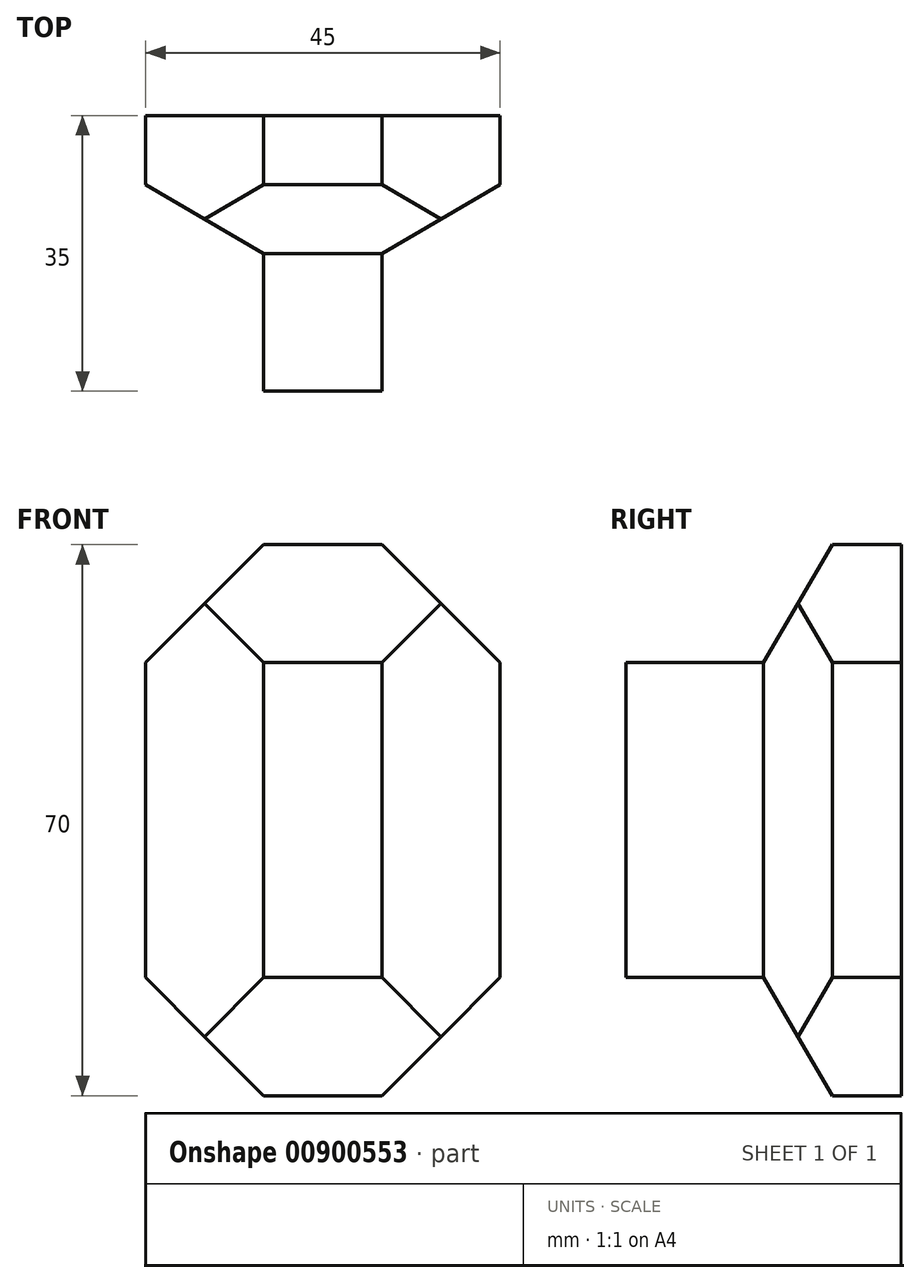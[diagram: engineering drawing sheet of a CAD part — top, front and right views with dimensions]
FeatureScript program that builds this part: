
annotation { "Feature Type Name" : "Feature", "Feature Type Description" : "" }
export const myFeature = defineFeature(function(context is Context, id is Id, definition is map)
    precondition{}
    {
        {
            var Q0;
            Q0=qCreatedBy(makeId("Top.planeOp"),FACE);
            var sketch = newSketch(context, id + "F0", { "sketchPlane" : qUnion([Q0])});
            skLineSegment(sketch, "E0.bottom", {"start": v(7.5, 17.5) * mm, "end": v(-7.5, 17.5) * mm});
            skLineSegment(sketch, "E0.top", {"start": v(7.5, -17.5) * mm, "end": v(-7.5, -17.5) * mm});
            skLineSegment(sketch, "E0.left", {"start": v(7.5, 17.5) * mm, "end": v(7.5, -17.5) * mm});
            skLineSegment(sketch, "E0.right", {"start": v(-7.5, 17.5) * mm, "end": v(-7.5, -17.5) * mm});
            skPoint(sketch, "E0.middle", {"position": v(0, 0) * mm});
            skLineSegment(sketch, "E1.bottom", {"start": v(-7.5, 17.5) * mm, "end": v(22.5, 17.5) * mm});
            skLineSegment(sketch, "E1.top", {"start": v(-7.5, 0) * mm, "end": v(22.5, 0) * mm});
            skLineSegment(sketch, "E1.left", {"start": v(-7.5, 17.5) * mm, "end": v(-7.5, 0) * mm});
            skLineSegment(sketch, "E1.right", {"start": v(22.5, 17.5) * mm, "end": v(22.5, 0) * mm});
            skLineSegment(sketch, "E2.bottom", {"start": v(7.5, 17.5) * mm, "end": v(-22.5, 17.5) * mm});
            skLineSegment(sketch, "E2.top", {"start": v(7.5, 0) * mm, "end": v(-22.5, 0) * mm});
            skLineSegment(sketch, "E2.left", {"start": v(7.5, 17.5) * mm, "end": v(7.5, 0) * mm});
            skLineSegment(sketch, "E2.right", {"start": v(-22.5, 17.5) * mm, "end": v(-22.5, 0) * mm});
            skLineSegment(sketch, "E3.bottom", {"start": v(-22.5, 17.5) * mm, "end": v(22.5, 17.5) * mm});
            skLineSegment(sketch, "E3.top", {"start": v(-22.5, 8.75) * mm, "end": v(22.5, 8.75) * mm});
            skLineSegment(sketch, "E3.left", {"start": v(-22.5, 17.5) * mm, "end": v(-22.5, 8.75) * mm});
            skLineSegment(sketch, "E3.right", {"start": v(22.5, 17.5) * mm, "end": v(22.5, 8.75) * mm});
            skLineSegment(sketch, "E4", {"start": v(-22.5, 8.75) * mm, "end": v(-7.5, 0) * mm});
            skLineSegment(sketch, "E5", {"start": v(22.5, 8.75) * mm, "end": v(7.5, 0) * mm});
            skSolve(sketch);
        }
        {
            var Q0;
            {var subQ0=sQuery(id+"F0.wireOp",EDGE,"E0.bottom");Q0=makeQuery(id+"F0.imprint","IMPRINT",FACE,{"disambiguationData":[TD([[makeQuery(id+"F0.imprint","IMPRINT",EDGE,{"derivedFrom":subQ0}),1.0]])]});}
            var Q1;
            {var subQ0=sQuery(id+"F0.wireOp",EDGE,"E0.top");Q1=makeQuery(id+"F0.imprint","IMPRINT",FACE,{"disambiguationData":[TD([[makeQuery(id+"F0.imprint","IMPRINT",EDGE,{"derivedFrom":subQ0}),-1.0]])]});}
            var Q2;
            {var subQ3=sQuery(id+"F0.wireOp",EDGE,"E3.top");var subQ5=sQuery(id+"F0.wireOp",EDGE,"E0.right");var subQ7=makeQuery(id+"F0.imprint","INTERSECT",VERTEX,{"derivedFrom":[subQ5,subQ3]});Q2=makeQuery(id+"F0.imprint","IMPRINT",FACE,{"disambiguationData":[TD([[makeQuery(id+"F0.imprint","IMPRINT",EDGE,{"disambiguationData":[TD([[subQ7,-1.0]])],"derivedFrom":subQ3}),-1.0]])]});}
            var Q3;
            {var subQ0=sQuery(id+"F0.wireOp",EDGE,"E1.bottom");Q3=makeQuery(id+"F0.imprint","IMPRINT",FACE,{"disambiguationData":[TD([[makeQuery(id+"F0.imprint","IMPRINT",EDGE,{"derivedFrom":subQ0}),-1.0]])]});}
            var Q4;
            {var subQ0=sQuery(id+"F0.wireOp",EDGE,"E5");Q4=makeQuery(id+"F0.imprint","IMPRINT",FACE,{"disambiguationData":[TD([[makeQuery(id+"F0.imprint","IMPRINT",EDGE,{"derivedFrom":subQ0}),-1.0]])]});}
            var Q5;
            {var subQ0=sQuery(id+"F0.wireOp",EDGE,"E2.bottom");Q5=makeQuery(id+"F0.imprint","IMPRINT",FACE,{"disambiguationData":[TD([[makeQuery(id+"F0.imprint","IMPRINT",EDGE,{"derivedFrom":subQ0}),1.0]])]});}
            var Q6;
            {var subQ0=sQuery(id+"F0.wireOp",EDGE,"E4");Q6=makeQuery(id+"F0.imprint","IMPRINT",FACE,{"disambiguationData":[TD([[makeQuery(id+"F0.imprint","IMPRINT",EDGE,{"derivedFrom":subQ0}),1.0]])]});}
            extrude(context, id + "F1", {"entities" : qUnion([Q0, Q1, Q2, Q3, Q4, Q5, Q6]), "depth" : 40 * mm, "offsetDistance" : 25 * mm});
        }
        {
            var Q0;
            {var subQ3=sQuery(id+"F0.wireOp",EDGE,"E3.top");var subQ5=sQuery(id+"F0.wireOp",EDGE,"E0.right");var subQ7=makeQuery(id+"F0.imprint","INTERSECT",VERTEX,{"derivedFrom":[subQ5,subQ3]});Q0=makeQuery(id+"F0.imprint","IMPRINT",FACE,{"disambiguationData":[TD([[makeQuery(id+"F0.imprint","IMPRINT",EDGE,{"disambiguationData":[TD([[subQ7,-1.0]])],"derivedFrom":subQ3}),-1.0]])]});}
            var Q1;
            {var subQ0=sQuery(id+"F0.wireOp",EDGE,"E0.bottom");Q1=makeQuery(id+"F0.imprint","IMPRINT",FACE,{"disambiguationData":[TD([[makeQuery(id+"F0.imprint","IMPRINT",EDGE,{"derivedFrom":subQ0}),1.0]])]});}
            extrude(context, id + "F2", {"entities" : qUnion([Q0, Q1]), "depth" : 55 * mm, "offsetDistance" : 25 * mm});
        }
        {
            var Q0;
            {var subQ3=sQuery(id+"F0.wireOp",EDGE,"E3.top");var subQ5=sQuery(id+"F0.wireOp",EDGE,"E0.right");var subQ7=makeQuery(id+"F0.imprint","INTERSECT",VERTEX,{"derivedFrom":[subQ5,subQ3]});Q0=makeQuery(id+"F0.imprint","IMPRINT",FACE,{"disambiguationData":[TD([[makeQuery(id+"F0.imprint","IMPRINT",EDGE,{"disambiguationData":[TD([[subQ7,-1.0]])],"derivedFrom":subQ3}),-1.0]])]});}
            var Q1;
            {var subQ0=sQuery(id+"F0.wireOp",EDGE,"E0.bottom");Q1=makeQuery(id+"F0.imprint","IMPRINT",FACE,{"disambiguationData":[TD([[makeQuery(id+"F0.imprint","IMPRINT",EDGE,{"derivedFrom":subQ0}),1.0]])]});}
            extrude(context, id + "F3", {"entities" : qUnion([Q0, Q1]), "oppositeDirection" : true, "depth" : 15 * mm, "offsetDistance" : 25 * mm});
        }
        {
            var Q0;
            Q0=makeQuery(id+"F2.opExtrude","SWEPT_BODY",BODY,{"disambiguationData":[OSD([sQuery(id+"F0.wireOp",EDGE,"E0.bottom"),sQuery(id+"F0.wireOp",EDGE,"E0.left"),sQuery(id+"F0.wireOp",EDGE,"E0.right"),sQuery(id+"F0.wireOp",EDGE,"E1.top")])]});
            var Q1;
            Q1=makeQuery(id+"F1.opExtrude","SWEPT_BODY",BODY,{"disambiguationData":[OSD([sQuery(id+"F0.wireOp",EDGE,"E0.bottom"),sQuery(id+"F0.wireOp",EDGE,"E0.top"),sQuery(id+"F0.wireOp",EDGE,"E0.left"),sQuery(id+"F0.wireOp",EDGE,"E0.right"),sQuery(id+"F0.wireOp",EDGE,"E1.bottom"),sQuery(id+"F0.wireOp",EDGE,"E1.right"),sQuery(id+"F0.wireOp",EDGE,"E2.bottom"),sQuery(id+"F0.wireOp",EDGE,"E2.right"),sQuery(id+"F0.wireOp",EDGE,"E4"),sQuery(id+"F0.wireOp",EDGE,"E5")])]});
            var Q2;
            Q2=makeQuery(id+"F3.opExtrude","SWEPT_BODY",BODY,{"disambiguationData":[OSD([sQuery(id+"F0.wireOp",EDGE,"E0.bottom"),sQuery(id+"F0.wireOp",EDGE,"E0.left"),sQuery(id+"F0.wireOp",EDGE,"E0.right"),sQuery(id+"F0.wireOp",EDGE,"E1.top")])]});
            booleanBodies(context, id + "F4", {"operationType" : BooleanOperationType.UNION, "tools" : qUnion([Q0, Q1, Q2])});
        }
        {
            var Q0;
            Q0=qCreatedBy(makeId("Right.planeOp"),FACE);
            var sketch = newSketch(context, id + "F5", { "sketchPlane" : qUnion([Q0])});
            skLineSegment(sketch, "E6", {"start": v(0, 0) * mm, "end": v(8.75, 0) * mm});
            skLineSegment(sketch, "E7", {"start": v(8.75, 0) * mm, "end": v(8.75, -15) * mm});
            skLineSegment(sketch, "E8", {"start": v(0, 0) * mm, "end": v(8.75, -15) * mm});
            skLineSegment(sketch, "E9", {"start": v(0, 0) * mm, "end": v(0, -15) * mm});
            skLineSegment(sketch, "E10", {"start": v(0, -15) * mm, "end": v(8.75, -15) * mm});
            skSolve(sketch);
        }
        {
            var Q0;
            Q0=makeQuery(id+"F2.opExtrude","SWEPT_BODY",BODY,{"disambiguationData":[OSD([sQuery(id+"F0.wireOp",EDGE,"E0.bottom"),sQuery(id+"F0.wireOp",EDGE,"E0.left"),sQuery(id+"F0.wireOp",EDGE,"E0.right"),sQuery(id+"F0.wireOp",EDGE,"E1.top")])]});
            transform(context, id + "F6", {"entities" : qUnion([Q0]), "transformType" : TransformType.TRANSLATION_3D, "dx" : 7.5 * mm, "dy" : 0 * mm, "dz" : 0 * mm, "makeCopy" : false});
        }
        {
            var Q0;
            Q0=makeQuery(id+"F5.imprint","IMPRINT",FACE,{"disambiguationData":[TD([[makeQuery(id+"F5.imprint","IMPRINT",EDGE,{"derivedFrom":sQuery(id+"F5.wireOp",EDGE,"E8")}),-1.0]])]});
            extrude(context, id + "F7", {"entities" : qUnion([Q0]), "operationType" : NewBodyOperationType.REMOVE, "depth" : 20.46 * mm, "offsetDistance" : 25 * mm});
        }
        {
            var Q0;
            Q0=makeQuery(id+"F2.opExtrude","SWEPT_BODY",BODY,{"disambiguationData":[OSD([sQuery(id+"F0.wireOp",EDGE,"E0.bottom"),sQuery(id+"F0.wireOp",EDGE,"E0.left"),sQuery(id+"F0.wireOp",EDGE,"E0.right"),sQuery(id+"F0.wireOp",EDGE,"E1.top")])]});
            var Q1;
            Q1=sQuery(id+"F0.wireOp",EDGE,"E0.left");
            transform(context, id + "F8", {"entities" : qUnion([Q0]), "transformType" : TransformType.ROTATION, "transformAxis" : qUnion([Q1]), "angle" : 180 * degree, "makeCopy" : false});
        }
        {
            var Q0;
            Q0=makeQuery(id+"F2.opExtrude","SWEPT_BODY",BODY,{"disambiguationData":[OSD([sQuery(id+"F0.wireOp",EDGE,"E0.bottom"),sQuery(id+"F0.wireOp",EDGE,"E0.left"),sQuery(id+"F0.wireOp",EDGE,"E0.right"),sQuery(id+"F0.wireOp",EDGE,"E1.top")])]});
            transform(context, id + "F9", {"entities" : qUnion([Q0]), "transformType" : TransformType.TRANSLATION_3D, "dx" : 0 * mm, "dy" : 0 * mm, "dz" : 40 * mm, "makeCopy" : false});
        }
        {
            var Q0;
            Q0=makeQuery(id+"F5.imprint","IMPRINT",FACE,{"disambiguationData":[TD([[makeQuery(id+"F5.imprint","IMPRINT",EDGE,{"derivedFrom":sQuery(id+"F5.wireOp",EDGE,"E8")}),-1.0]])]});
            extrude(context, id + "F10", {"entities" : qUnion([Q0]), "operationType" : NewBodyOperationType.REMOVE, "depth" : 25 * mm, "offsetDistance" : 25 * mm});
        }
        {
            var Q0;
            Q0=makeQuery(id+"F3.opExtrude","CAP_EDGE",EDGE,{"disambiguationData":[OSD([sQuery(id+"F0.wireOp",EDGE,"E0.right")])],"isStart":true});
            var Q1;
            Q1=makeQuery(id+"F3.opExtrude","CAP_EDGE",EDGE,{"disambiguationData":[OSD([sQuery(id+"F0.wireOp",EDGE,"E0.left")])],"isStart":true});
            var Q2;
            {var subQ0=sQuery(id+"F0.wireOp",EDGE,"E0.left");Q2=makeQuery(id+"F4.opBoolean","INTERSECT",EDGE,{"derivedFrom":[makeQuery(id+"F1.opExtrude","CAP_FACE",FACE,{"disambiguationData":[OSD([sQuery(id+"F0.wireOp",EDGE,"E0.bottom"),sQuery(id+"F0.wireOp",EDGE,"E0.top"),subQ0,sQuery(id+"F0.wireOp",EDGE,"E0.right"),sQuery(id+"F0.wireOp",EDGE,"E1.bottom"),sQuery(id+"F0.wireOp",EDGE,"E1.right"),sQuery(id+"F0.wireOp",EDGE,"E2.bottom"),sQuery(id+"F0.wireOp",EDGE,"E2.right"),sQuery(id+"F0.wireOp",EDGE,"E4"),sQuery(id+"F0.wireOp",EDGE,"E5")])],"isStart":false}),makeQuery(id+"F2.opExtrude","SWEPT_FACE",FACE,{"disambiguationData":[OSD([subQ0])]})]});}
            var Q3;
            {var subQ0=sQuery(id+"F0.wireOp",EDGE,"E0.right");Q3=makeQuery(id+"F4.opBoolean","INTERSECT",EDGE,{"derivedFrom":[makeQuery(id+"F1.opExtrude","CAP_FACE",FACE,{"disambiguationData":[OSD([sQuery(id+"F0.wireOp",EDGE,"E0.bottom"),sQuery(id+"F0.wireOp",EDGE,"E0.top"),sQuery(id+"F0.wireOp",EDGE,"E0.left"),subQ0,sQuery(id+"F0.wireOp",EDGE,"E1.bottom"),sQuery(id+"F0.wireOp",EDGE,"E1.right"),sQuery(id+"F0.wireOp",EDGE,"E2.bottom"),sQuery(id+"F0.wireOp",EDGE,"E2.right"),sQuery(id+"F0.wireOp",EDGE,"E4"),sQuery(id+"F0.wireOp",EDGE,"E5")])],"isStart":false}),makeQuery(id+"F2.opExtrude","SWEPT_FACE",FACE,{"disambiguationData":[OSD([subQ0])]})]});}
            chamfer(context, id + "F11", {"entities" : qUnion([Q0, Q1, Q2, Q3]), "width" : 15 * mm, "tangentPropagation" : true});
        }
    });
